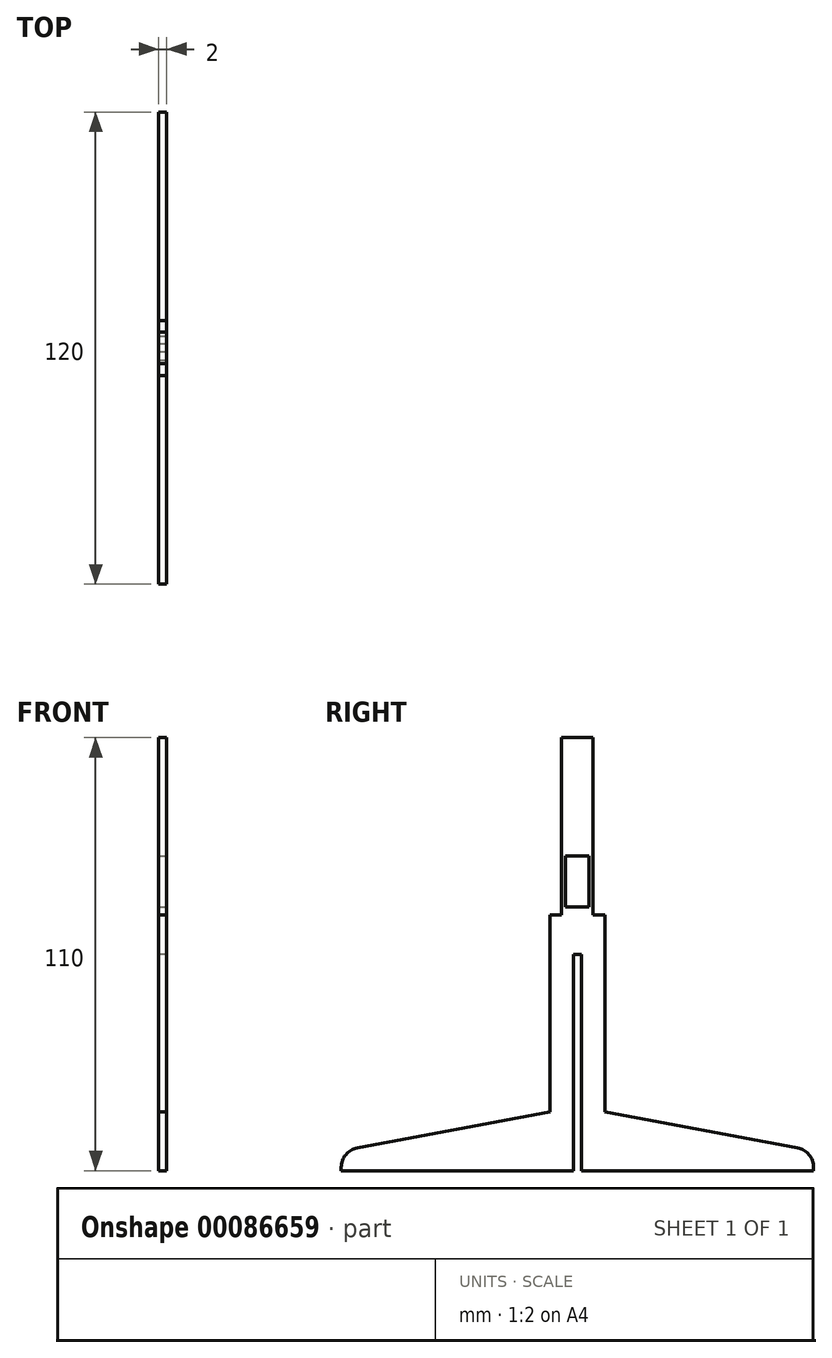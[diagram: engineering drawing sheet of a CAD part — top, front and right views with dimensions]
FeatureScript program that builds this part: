
annotation { "Feature Type Name" : "Feature", "Feature Type Description" : "" }
export const myFeature = defineFeature(function(context is Context, id is Id, definition is map)
    precondition{}
    {
        {
            var Q0;
            Q0=qCreatedBy(makeId("Right.planeOp"),FACE);
            var sketch = newSketch(context, id + "F0", { "sketchPlane" : qUnion([Q0])});
            skLineSegment(sketch, "E0", {"start": v(-60, 0) * mm, "end": v(-1, 0) * mm});
            skLineSegment(sketch, "E1", {"start": v(-1, 0) * mm, "end": v(-1, 55) * mm});
            skLineSegment(sketch, "E2", {"start": v(-1, 55) * mm, "end": v(1, 55) * mm});
            skLineSegment(sketch, "E3", {"start": v(1, 55) * mm, "end": v(1, 0) * mm});
            skLineSegment(sketch, "E4", {"start": v(1, 0) * mm, "end": v(60, 0) * mm});
            skLineSegment(sketch, "E5", {"start": v(7, 15) * mm, "end": v(7, 65) * mm});
            skLineSegment(sketch, "E6", {"start": v(7, 65) * mm, "end": v(4, 65) * mm});
            skLineSegment(sketch, "E7", {"start": v(4, 65) * mm, "end": v(4, 110) * mm});
            skLineSegment(sketch, "E8", {"start": v(4, 110) * mm, "end": v(-4, 110) * mm});
            skLineSegment(sketch, "E9", {"start": v(-4, 110) * mm, "end": v(-4, 65) * mm});
            skLineSegment(sketch, "E10", {"start": v(-4, 65) * mm, "end": v(-7, 65) * mm});
            skLineSegment(sketch, "E11", {"start": v(-7, 65) * mm, "end": v(-7, 15) * mm});
            skLineSegment(sketch, "E12", {"start": v(7, 15) * mm, "end": v(60, 5) * mm});
            skLineSegment(sketch, "E13", {"start": v(60, 5) * mm, "end": v(60, 0) * mm});
            skLineSegment(sketch, "E14", {"start": v(-7, 15) * mm, "end": v(-60, 5) * mm});
            skLineSegment(sketch, "E15", {"start": v(-60, 5) * mm, "end": v(-60, 0) * mm});
            skSolve(sketch);
        }
        {
            var Q0;
            Q0=makeQuery(id+"F0.imprint","IMPRINT",FACE,{"disambiguationData":[TD([[makeQuery(id+"F0.imprint","IMPRINT",EDGE,{"derivedFrom":sQuery(id+"F0.wireOp",EDGE,"E0")}),1.0]])]});
            extrude(context, id + "F1", {"entities" : qUnion([Q0]), "depth" : 1 * mm, "hasSecondDirection" : true, "secondDirectionOppositeDirection" : true, "secondDirectionDepth" : 1 * mm});
        }
        {
            var Q0;
            Q0=makeQuery(id+"F1.opExtrude","CAP_FACE",FACE,{"disambiguationData":[OSD([sQuery(id+"F0.wireOp",EDGE,"E0"),sQuery(id+"F0.wireOp",EDGE,"E1"),sQuery(id+"F0.wireOp",EDGE,"E2"),sQuery(id+"F0.wireOp",EDGE,"E3"),sQuery(id+"F0.wireOp",EDGE,"E4"),sQuery(id+"F0.wireOp",EDGE,"NnTkz0Dv-VUkw-y3kH-THcp-3fUy8kmgUzWu"),sQuery(id+"F0.wireOp",EDGE,"E5"),sQuery(id+"F0.wireOp",EDGE,"E6"),sQuery(id+"F0.wireOp",EDGE,"E7"),sQuery(id+"F0.wireOp",EDGE,"E8"),sQuery(id+"F0.wireOp",EDGE,"E9"),sQuery(id+"F0.wireOp",EDGE,"E10"),sQuery(id+"F0.wireOp",EDGE,"E11"),sQuery(id+"F0.wireOp",EDGE,"P84eyzt6-VuVA-ecCy-TwQ4-GEdNslctG4jy")])],"isStart":false});
            var sketch = newSketch(context, id + "F2", { "sketchPlane" : qUnion([Q0])});
            skLineSegment(sketch, "E16", {"start": v(-3, 80) * mm, "end": v(3, 80) * mm});
            skLineSegment(sketch, "E17", {"start": v(3, 80) * mm, "end": v(3, 67) * mm});
            skLineSegment(sketch, "E18", {"start": v(3, 67) * mm, "end": v(-3, 67) * mm});
            skLineSegment(sketch, "E19", {"start": v(-3, 67) * mm, "end": v(-3, 80) * mm});
            skSolve(sketch);
        }
        {
            var Q0;
            Q0=makeQuery(id+"F2.imprint","IMPRINT",FACE,{"disambiguationData":[TD([[makeQuery(id+"F2.imprint","IMPRINT",EDGE,{"derivedFrom":sQuery(id+"F2.wireOp",EDGE,"E16")}),-1.0]])]});
            extrude(context, id + "F3", {"entities" : qUnion([Q0]), "operationType" : NewBodyOperationType.REMOVE, "oppositeDirection" : true, "depth" : 2 * mm, "hasSecondDirection" : true, "secondDirectionOppositeDirection" : false, "secondDirectionDepth" : 2 * mm});
        }
        {
            var Q0;
            Q0=makeQuery(id+"F1.opExtrude","SWEPT_EDGE",EDGE,{"disambiguationData":[OSD([sQuery(id+"F0.wireOp",EDGE,"E14"),sQuery(id+"F0.wireOp",EDGE,"E15")])]});
            var Q1;
            Q1=makeQuery(id+"F1.opExtrude","SWEPT_EDGE",EDGE,{"disambiguationData":[OSD([sQuery(id+"F0.wireOp",EDGE,"E12"),sQuery(id+"F0.wireOp",EDGE,"E13")])]});
            fillet(context, id + "F4", {"entities" : qUnion([Q0, Q1]), "radius" : 5 * mm, "tangentPropagation" : true, "allowEdgeOverflow" : false});
        }
    });
